# Revit family: svetilnik_alfresco_strit-b_dtu-08_os_i_dtu-08_ossv
name_source: partatom
category: Осветительные приборы
revit_build: Autodesk Revit 2016 (Build: 20150714_1515(x64)
units: mm (PartAtom-declared; Revit-internal decimal feet)

## family parameters
Всегда вертикально = Да
Источник света = Да
На основе рабочей плоскости = Нет
Общий = Нет
При загрузке вырезать с полостями = Нет
Размер круглого соединителя = Использовать диаметр
Тип детали = Нормальный
Точка расчета площади = Нет

## types (4) — shared parameters
ADSK_Единица измерения = шт
ADSK_Классификация нагрузок = Освещение
ADSK_Количество фаз = 2
ADSK_Количество фаз числовое = 2
ADSK_Коэффициент мощности = 0.97
ADSK_Напряжение = 220 В
ADSK_Размер_Высота = 4215 мм
ADSK_Размер_Длина = 500 мм
ADSK_Размер_Ширина = 500 мм
ADSK_Ток = 0 А
ADSK_Энергоэффективность = 120 лм/Вт
Dсв = 120 мм
IP Class = IP 65
URL = http://www.allfresco.ru
Блок аварийного питания = Нет
Видимая форма излучения при визуализации = Нет
Изготовитель = ALFRESCO
Излучение по диаметру окружности = 120 мм
Класс Защиты = 1
Класс пожароопасности = F (светильники предназначены для установки непосредственно на поверхность из нормально воспламеняемых матеоиалов)
Климатическая зона = УХЛ1
Материал опоры = Сталь, окрашенная, черная
Область использования = Ландшафт, коттедж.поселки,микрорайоны,АЗС, автостоянки
Светофильтр = 16777215
Сечение по фланцу = 240 мм
Смещение цветовой температуры при затухании лампы = <Нет>
Температура эксплуатации = -35 +40
Тип ИС = LED-светодиоды
Тип КСС = Sym
Тип ПРА = -
Тип продукции = Комплект(Опора освещения+LED светильник)
Угол наклона = 90.00°
Цветовая температура = 3000-5500

## per-type parameters (varying)
| type | ADSK_Артикул | ADSK_Масса | ADSK_Модель | ADSK_Наименование | ADSK_Номинальная мощность | ADSK_Полная мощность | Dопв | Dопн | Полная установленная мощность | Световой поток | Файл фотометрической сетки |
| Стрит В (ДТУ-08, ОС) 30Вт | 1105001040 | 36 | Стрит-А(ДТУ-07, ОС) | Стрит В (ДТУ-08, ОС) 30Вт - св-к ДТУ-08-AF (02, PC прозр., Ш черное) на опоре ОС 3,6 ЧС | 30 Вт | 31 В·А | 102 мм | 102 мм | 31 В·А | 4200 лм | ДТУ-08-AF Street B 30W.ies |
| Стрит В (ДТУ-08, ОССв) 30Вт | 1105001251 | 35 | Стрит-В (ДТУ-08, ОССв) | Стрит В (ДТУ-08, ОССв) 30Вт - св-к ДТУ-08-AF (02, PC прозр., Ш черное)  на опоре ОССв 3,6 ЧС | 30 Вт | 31 В·А | 76 мм | 114 мм | 31 В·А | 4200 лм | ДТУ-08-AF Street B 30W.ies |
| Стрит В (ДТУ-08, ОС) 50Вт | 1105002240 | 37 | Стрит-В (ДТУ-08, ОС) | Стрит В (ДТУ-08, ОС) 50Вт - св-к ДТУ-08-AF (02, PC прозр., Ш черное) на опоре ОС 3,6 ЧС | 50 Вт | 52 В·А | 102 мм | 102 мм | 52 В·А | 6000 лм | ДТУ-08-AF Street B 50W.ies |
| Стрит В (ДТУ-08, ОССв) 50Вт | 1105002250 | 36 | Стрит-В (ДТУ-08, ОССв) | Стрит В (ДТУ-08, ОССв) 50Вт - св-к ДТУ-08-AF (02, PC прозр., Ш черное)  на опоре ОССв 3,6 ЧС | 50 Вт | 52 В·А | 76 мм | 114 мм | 52 В·А | 6000 лм | ДТУ-08-AF Street B 50W.ies |

## geometry (parser evidence)
native form markers: Blend x147
no freeform markers — native parametric forms only
